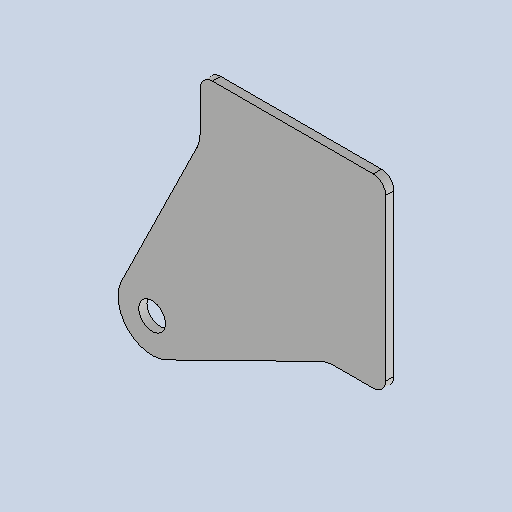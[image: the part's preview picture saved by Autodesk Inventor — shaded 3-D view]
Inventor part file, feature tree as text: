
AUTODESK INVENTOR PART (.ipt)
format: ipt  version: 2025 (Build 290162010, 162A)  size: 201,216 bytes
history: native  units: mm
features: other x2, sheet_metal_op x1, chamfer x1, sketch x1
ambient origin geometry x8: Origin, YZ Plane, XZ Plane, XY Plane, X Axis, Y Axis, Z Axis, Center Point
bodies: Solid1 (feature_tree)
feature tree (5):
  sheet_metal_op  "Face1"
  chamfer  "Corner Round3"
  sketch  "Sketch1"  dims[d2=80.0mm d3=80.0mm d6=4.0mm d29=5.0mm d30=13.0mm d31=10.0mm d32=40.0mm d34=5.0mm d35=15.0mm d36=25.0mm d37=6.0mm]
  other  "Plate1"
  other  "Definition1"
